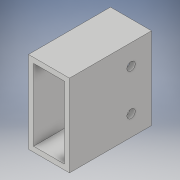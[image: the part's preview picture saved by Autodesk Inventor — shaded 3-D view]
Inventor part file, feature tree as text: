
AUTODESK INVENTOR PART (.ipt)
format: ipt  version: 2018 (Build 220112000, 112)  size: 109,568 bytes
history: native  units: in
note: dims shown in document units (in); Inventor stores cm internally (conversion verified against a paired STEP export)
features: extrude x2, sketch x2
ambient origin geometry x8: Origin, YZ Plane, XZ Plane, XY Plane, X Axis, Y Axis, Z Axis, Center Point
bodies: Solid1 (feature_tree)
feature tree (4):
  extrude  "Extrusion1"  Depth=2.0in
  extrude  "Extrusion2"  Depth=2.0in TaperAngle=0.0deg
  sketch  "Sketch1"  dims[d0=1.0in d1=2.0in]
  sketch  "Sketch2"  dims[d2=0.125in d3=2.0in d4=0.0in d5=0.5in d6=0.5in d7=1.0in d8=0.2031in d9=2.0in d10=0.0in]
